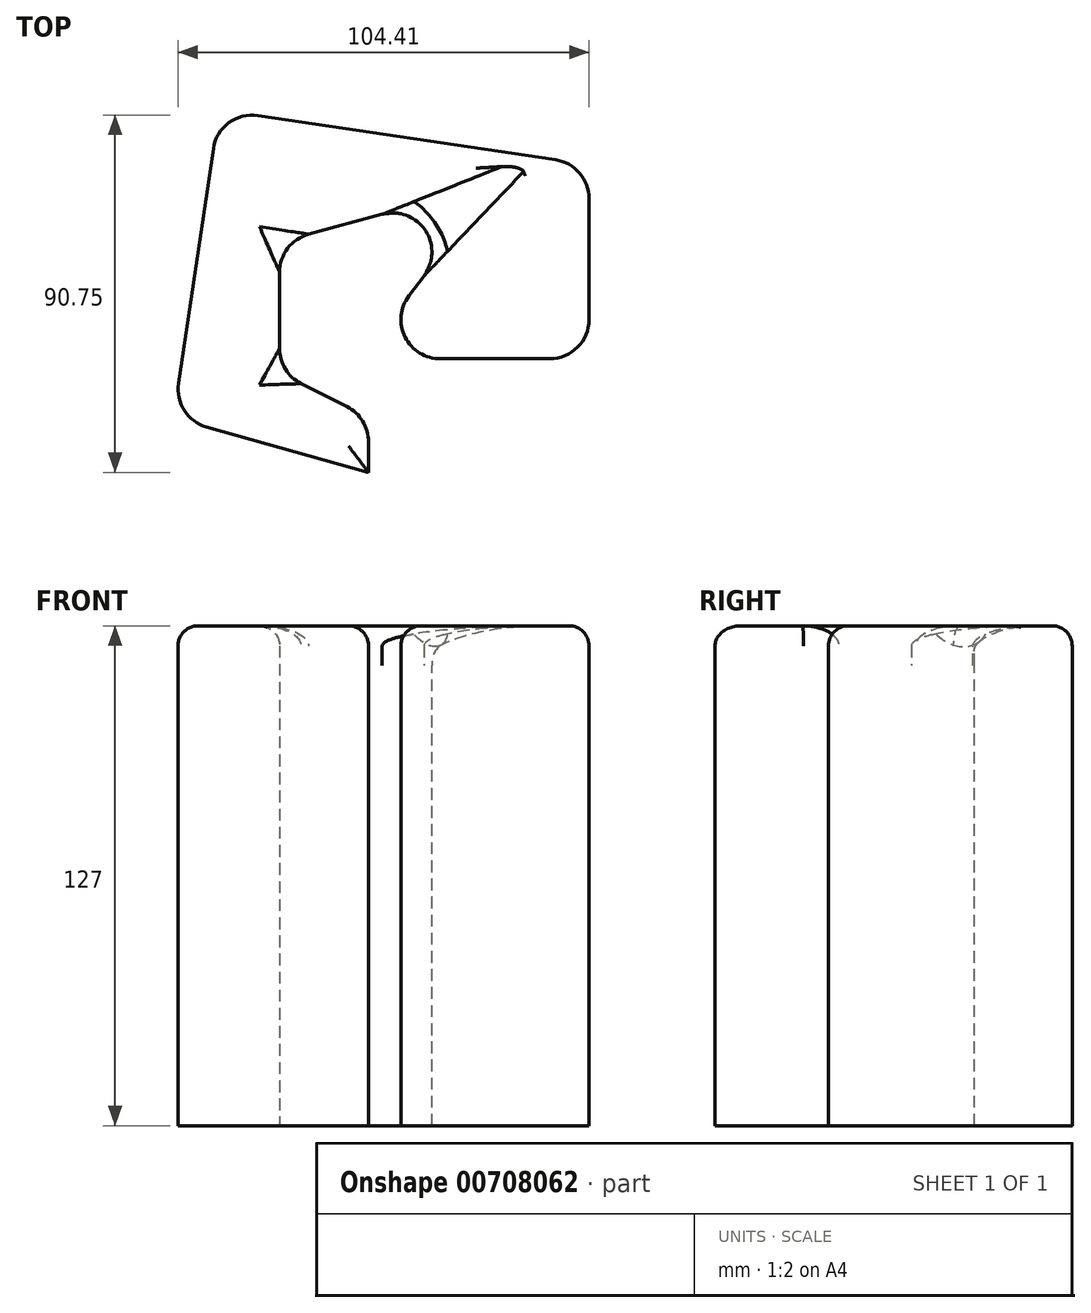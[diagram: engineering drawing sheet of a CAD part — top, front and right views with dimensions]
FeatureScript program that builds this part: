
annotation { "Feature Type Name" : "Feature", "Feature Type Description" : "" }
export const myFeature = defineFeature(function(context is Context, id is Id, definition is map)
    precondition{}
    {
        {
            var Q0;
            Q0=qCreatedBy(makeId("Top.planeOp"),FACE);
            var sketch = newSketch(context, id + "F0", { "sketchPlane" : qUnion([Q0])});
            skLineSegment(sketch, "E0", {"start": v(42.94, 10.58) * mm, "end": v(42.94, -29.67) * mm});
            skLineSegment(sketch, "E1", {"start": v(42.94, -29.67) * mm, "end": v(-14.94, -29.67) * mm});
            skLineSegment(sketch, "E2", {"start": v(-14.94, -29.67) * mm, "end": v(18.67, 14.73) * mm});
            skLineSegment(sketch, "E3", {"start": v(18.67, 14.73) * mm, "end": v(-35.68, 0) * mm});
            skLineSegment(sketch, "E4", {"start": v(-35.68, 0) * mm, "end": v(-35.68, -33.2) * mm});
            skLineSegment(sketch, "E5", {"start": v(-35.68, -33.2) * mm, "end": v(-13.07, -44.6) * mm});
            skLineSegment(sketch, "E6", {"start": v(-13.07, -44.6) * mm, "end": v(-13.07, -58.5) * mm});
            skLineSegment(sketch, "E7", {"start": v(-13.07, -58.5) * mm, "end": v(-62.65, -44.6) * mm});
            skLineSegment(sketch, "E8", {"start": v(-62.65, -44.6) * mm, "end": v(-51.03, 33.6) * mm});
            skLineSegment(sketch, "E9", {"start": v(-51.03, 33.6) * mm, "end": v(42.94, 19.65) * mm});
            skLineSegment(sketch, "E10", {"start": v(42.94, 19.65) * mm, "end": v(42.94, 10.58) * mm});
            skSolve(sketch);
        }
        {
            var Q0;
            Q0=makeQuery(id+"F0.imprint","IMPRINT",FACE,{"disambiguationData":[TD([[makeQuery(id+"F0.imprint","IMPRINT",EDGE,{"derivedFrom":sQuery(id+"F0.wireOp",EDGE,"E0")}),-1.0]])]});
            extrude(context, id + "F1", {"entities" : qUnion([Q0]), "depth" : 127 * mm, "offsetDistance" : 25.4 * mm});
        }
        {
            var Q0;
            Q0=makeQuery(id+"F1.opExtrude","CAP_EDGE",EDGE,{"disambiguationData":[OSD([sQuery(id+"F0.wireOp",EDGE,"E9")])],"isStart":false});
            var Q1;
            Q1=makeQuery(id+"F1.opExtrude","CAP_EDGE",EDGE,{"disambiguationData":[OSD([sQuery(id+"F0.wireOp",EDGE,"E2")])],"isStart":false});
            var Q2;
            Q2=makeQuery(id+"F1.opExtrude","CAP_EDGE",EDGE,{"disambiguationData":[OSD([sQuery(id+"F0.wireOp",EDGE,"E8")])],"isStart":false});
            var Q3;
            Q3=makeQuery(id+"F1.opExtrude","CAP_EDGE",EDGE,{"disambiguationData":[OSD([sQuery(id+"F0.wireOp",EDGE,"E1")])],"isStart":false});
            var Q4;
            Q4=makeQuery(id+"F1.opExtrude","CAP_EDGE",EDGE,{"disambiguationData":[OSD([sQuery(id+"F0.wireOp",EDGE,"E5")])],"isStart":false});
            var Q5;
            Q5=makeQuery(id+"F1.opExtrude","CAP_EDGE",EDGE,{"disambiguationData":[OSD([sQuery(id+"F0.wireOp",EDGE,"E4")])],"isStart":false});
            var Q6;
            Q6=makeQuery(id+"F1.opExtrude","CAP_EDGE",EDGE,{"disambiguationData":[OSD([sQuery(id+"F0.wireOp",EDGE,"E3")])],"isStart":false});
            var Q7;
            Q7=makeQuery(id+"F1.opExtrude","CAP_EDGE",EDGE,{"disambiguationData":[OSD([sQuery(id+"F0.wireOp",EDGE,"E7")])],"isStart":false});
            var Q8;
            Q8=makeQuery(id+"F1.opExtrude","CAP_EDGE",EDGE,{"disambiguationData":[OSD([sQuery(id+"F0.wireOp",EDGE,"E6")])],"isStart":false});
            var Q9;
            Q9=makeQuery(id+"F1.opExtrude","CAP_EDGE",EDGE,{"disambiguationData":[OSD([sQuery(id+"F0.wireOp",EDGE,"E0"),sQuery(id+"F0.wireOp",EDGE,"E10")])],"isStart":false});
            fillet(context, id + "F2", {"entities" : qUnion([Q0, Q1, Q2, Q3, Q4, Q5, Q6, Q7, Q8, Q9]), "radius" : 5.08 * mm, "tangentPropagation" : true, "allowEdgeOverflow" : false});
        }
        {
            var Q0;
            Q0=makeQuery(id+"F1.opExtrude","SWEPT_EDGE",EDGE,{"disambiguationData":[OSD([sQuery(id+"F0.wireOp",EDGE,"E7"),sQuery(id+"F0.wireOp",EDGE,"E8")])]});
            var Q1;
            Q1=makeQuery(id+"F1.opExtrude","SWEPT_EDGE",EDGE,{"disambiguationData":[OSD([sQuery(id+"F0.wireOp",EDGE,"E8"),sQuery(id+"F0.wireOp",EDGE,"E9")])]});
            var Q2;
            Q2=makeQuery(id+"F1.opExtrude","SWEPT_EDGE",EDGE,{"disambiguationData":[OSD([sQuery(id+"F0.wireOp",EDGE,"E9"),sQuery(id+"F0.wireOp",EDGE,"E10")])]});
            var Q3;
            Q3=makeQuery(id+"F1.opExtrude","SWEPT_EDGE",EDGE,{"disambiguationData":[OSD([sQuery(id+"F0.wireOp",EDGE,"E0"),sQuery(id+"F0.wireOp",EDGE,"E1")])]});
            var Q4;
            Q4=makeQuery(id+"F1.opExtrude","SWEPT_EDGE",EDGE,{"disambiguationData":[OSD([sQuery(id+"F0.wireOp",EDGE,"E1"),sQuery(id+"F0.wireOp",EDGE,"E2")])]});
            var Q5;
            Q5=makeQuery(id+"F1.opExtrude","SWEPT_EDGE",EDGE,{"disambiguationData":[OSD([sQuery(id+"F0.wireOp",EDGE,"E2"),sQuery(id+"F0.wireOp",EDGE,"E3")])]});
            var Q6;
            Q6=makeQuery(id+"F1.opExtrude","SWEPT_EDGE",EDGE,{"disambiguationData":[OSD([sQuery(id+"F0.wireOp",EDGE,"E5"),sQuery(id+"F0.wireOp",EDGE,"E6")])]});
            var Q7;
            Q7=makeQuery(id+"F1.opExtrude","SWEPT_EDGE",EDGE,{"disambiguationData":[OSD([sQuery(id+"F0.wireOp",EDGE,"E3"),sQuery(id+"F0.wireOp",EDGE,"E4")])]});
            var Q8;
            Q8=makeQuery(id+"F1.opExtrude","SWEPT_EDGE",EDGE,{"disambiguationData":[OSD([sQuery(id+"F0.wireOp",EDGE,"E4"),sQuery(id+"F0.wireOp",EDGE,"E5")])]});
            fillet(context, id + "F3", {"entities" : qUnion([Q0, Q1, Q2, Q3, Q4, Q5, Q6, Q7, Q8]), "radius" : 10 * mm, "tangentPropagation" : true, "allowEdgeOverflow" : false});
        }
    });
